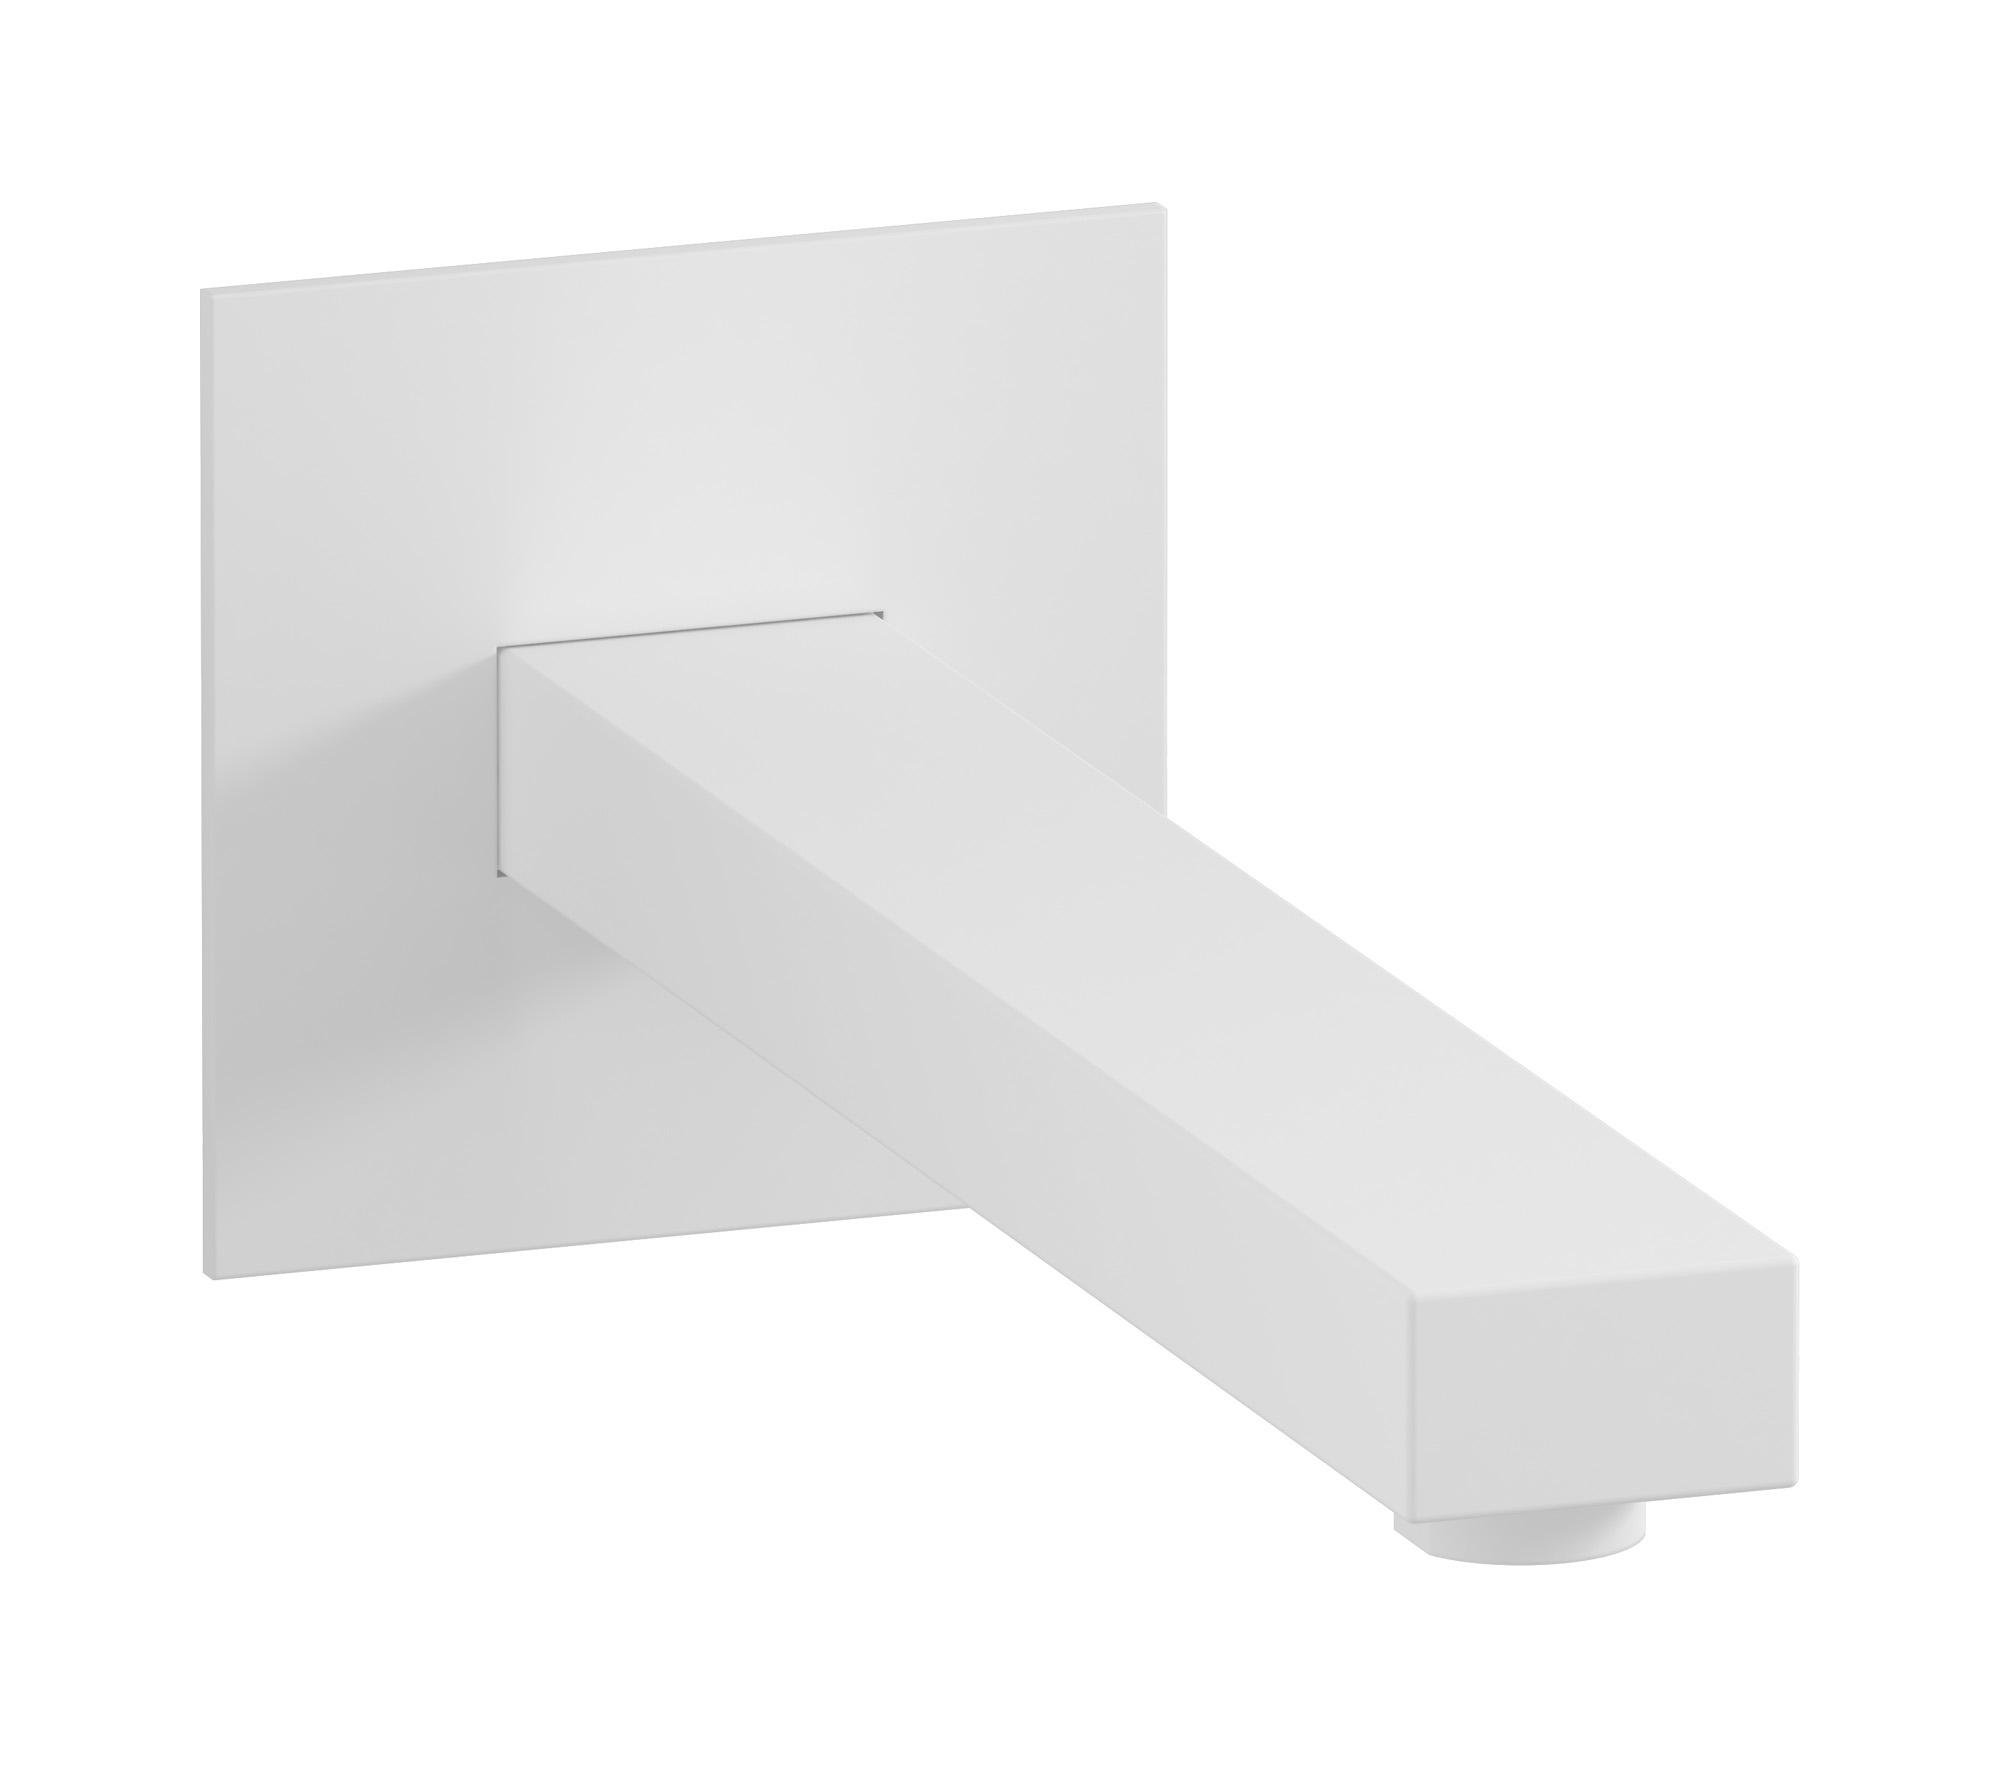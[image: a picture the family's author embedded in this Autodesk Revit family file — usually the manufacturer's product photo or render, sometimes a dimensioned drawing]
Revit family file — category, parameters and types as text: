
# Revit family: RU322
name_source: partatom
category: Apparecchi idraulici
units: mm (PartAtom-declared; Revit-internal decimal feet)

## family parameters
Basato su piano di lavoro = No
Condiviso = No
Mantieni orientamento annotazione = No
Numero OmniClass = 23.45.55.17
Punto di calcolo locali = No
Quota connettore circolare = Usa diametro
Sempre verticale = Sì
Taglio con vuoti quando caricato = No
Tipo di parte = Normale
Titolo OmniClass = Mixing Faucets

## types (12) — shared parameters
Commenti sul tipo = Long wall mounted spout
Connessione CW = No
Connessione HW = No
Connessione di scarico = No
Connessione di ventilazione = No
Descrizione = Long wall mounted spout
Produttore = IB Rubinetterie S.p.A.
URL = https://www.weareib.it
Water inlet = 10 mm  [stored 0.0328084 ft]
zero-valued in all types: Prospetto di default

## per-type parameters (varying)
| type | Finishes surface | Immagine tipo | Modello |
| Chrome | IB_Chrome | RU322CC.jpg | RU322CC |
| Matt White | IB_matt white | RU322BO.jpg | RU322BO |
| Black Chrome | IB_Black chrome | RU322CF.jpg | RU322CF |
| Brushed Black Chrome | IB_Brushed black chrome | RU322CS.jpg | RU322CS |
| Pale Gold | IB_Pale gold | RU322II.jpg | RU322II |
| Brushed Pale Gold | IB_brushed pale gold | RU322IS.jpg | RU322IS |
| Matt Black | IB_matt black | RU322NP.jpg | RU322NP |
| Gold | IB_gold | RU322OO.jpg | RU322OO |
| Brushed Gold | IB_brushed gold | RU322OS.jpg | RU322OS |
| Rose Gold | IB_Rose gold | RU322RS.jpg | RU322RS |
| Brushed Rose Gold | IB_Brushed rose gold | RU322SR.jpg | RU322SR |
| Brushed Nickel | IB_Brushed nickel | RU322SS.jpg | RU322SS |

note: [stored X ft] marks values corroborated as IEEE doubles in the binary element streams (Revit-internal decimal feet)
